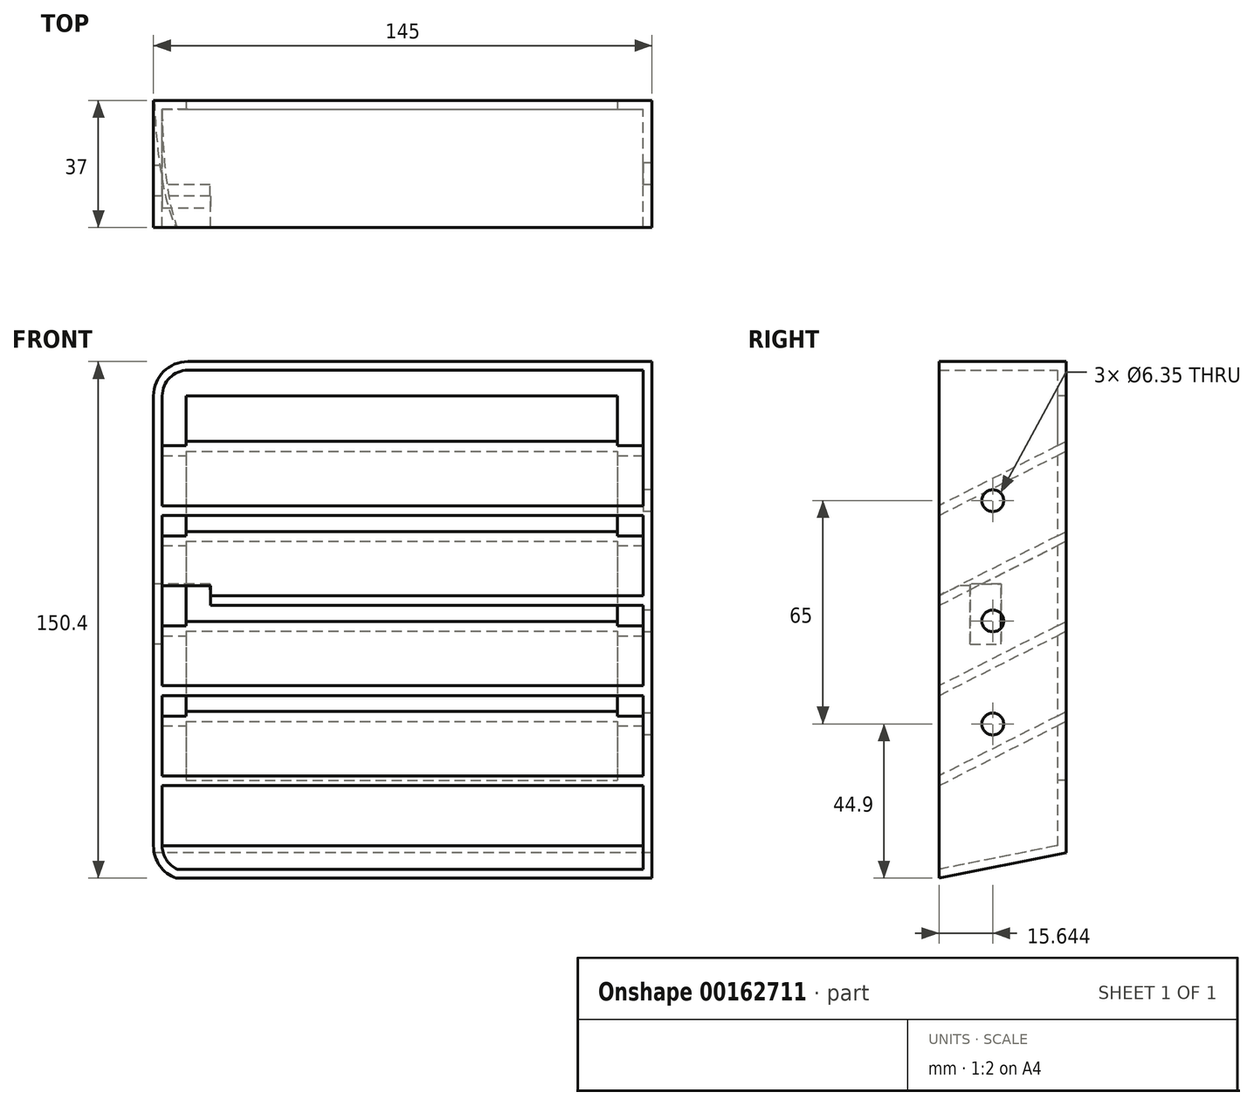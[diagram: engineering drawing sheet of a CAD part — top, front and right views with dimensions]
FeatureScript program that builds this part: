
annotation { "Feature Type Name" : "Feature", "Feature Type Description" : "" }
export const myFeature = defineFeature(function(context is Context, id is Id, definition is map)
    precondition{}
    {
        {
            var Q0;
            Q0=qCreatedBy(makeId("Front.planeOp"),FACE);
            var sketch = newSketch(context, id + "F0", { "sketchPlane" : qUnion([Q0])});
            skLineSegment(sketch, "E0.bottom", {"start": v(-62.5, 75.5) * mm, "end": v(72.5, 75.5) * mm});
            skLineSegment(sketch, "E0.top", {"start": v(-62.5, -75.5) * mm, "end": v(72.5, -75.5) * mm});
            skLineSegment(sketch, "E0.left", {"start": v(-72.5, 65.5) * mm, "end": v(-72.5, -65.5) * mm});
            skLineSegment(sketch, "E0.right", {"start": v(72.5, 75.5) * mm, "end": v(72.5, -75.5) * mm});
            skPoint(sketch, "E0.middle", {"position": v(0, 0) * mm});
            skPoint(sketch, "E1.visualSharp", {"position": v(72.5, 75.5) * mm});
            skPoint(sketch, "E2.visualSharp", {"position": v(72.5, -75.5) * mm});
            skPoint(sketch, "E3.visualSharp", {"position": v(-72.5, 75.5) * mm});
            skArc(sketch, "E3.filletArc", {"start": v(-62.5, 75.5) * mm, "mid": v(-69.57, 72.57) * mm, "end": v(-72.5, 65.5) * mm});
            skPoint(sketch, "E4.visualSharp", {"position": v(-72.5, -75.5) * mm});
            skArc(sketch, "E4.filletArc", {"start": v(-72.5, -65.5) * mm, "mid": v(-69.57, -72.57) * mm, "end": v(-62.5, -75.5) * mm});
            skSolve(sketch);
        }
        {
            var Q0;
            Q0=qSketchRegion(id+"F0",true);
            extrude(context, id + "F1", {"entities" : qUnion([Q0]), "depth" : 37 * mm});
        }
        {
            var Q0;
            Q0=makeQuery(id+"F1.opExtrude","CAP_EDGE",EDGE,{"disambiguationData":[OSD([sQuery(id+"F0.wireOp",EDGE,"E0.top")])],"isStart":true});
            chamfer(context, id + "F2", {"entities" : qUnion([Q0]), "chamferType" : ChamferType.TWO_OFFSETS, "width1" : 40 * mm, "oppositeDirection" : false, "width2" : 8 * mm});
        }
        {
            var Q0;
            Q0=makeQuery(id+"F1.opExtrude","CAP_FACE",FACE,{"disambiguationData":[OSD([sQuery(id+"F0.wireOp",EDGE,"E0.bottom"),sQuery(id+"F0.wireOp",EDGE,"E0.top"),sQuery(id+"F0.wireOp",EDGE,"E0.left"),sQuery(id+"F0.wireOp",EDGE,"E0.right"),sQuery(id+"F0.wireOp",EDGE,"E1.filletArc"),sQuery(id+"F0.wireOp",EDGE,"E2.filletArc")])],"isStart":false});
            shell(context, id + "F3", {"entities" : qUnion([Q0]), "thickness" : 2.54 * mm});
        }
        {
            var Q0;
            Q0=makeQuery(id+"F3.opShell","OFFSET_FACE",FACE,{"disambiguationData":[OSD([sQuery(id+"F0.wireOp",EDGE,"E0.bottom"),sQuery(id+"F0.wireOp",EDGE,"E0.top"),sQuery(id+"F0.wireOp",EDGE,"E0.left"),sQuery(id+"F0.wireOp",EDGE,"E0.right"),sQuery(id+"F0.wireOp",EDGE,"E1.filletArc"),sQuery(id+"F0.wireOp",EDGE,"E2.filletArc")])]});
            var sketch = newSketch(context, id + "F4", { "sketchPlane" : qUnion([Q0])});
            skPoint(sketch, "E5.middle", {"position": v(0, 0) * mm});
            skLineSegment(sketch, "E6.bottom", {"start": v(-63.05, 65.5) * mm, "end": v(62.5, 65.5) * mm});
            skLineSegment(sketch, "E6.top", {"start": v(-63.05, -46.42) * mm, "end": v(62.5, -46.42) * mm});
            skLineSegment(sketch, "E6.left", {"start": v(-63.05, 65.5) * mm, "end": v(-63.05, -46.42) * mm});
            skLineSegment(sketch, "E6.right", {"start": v(62.5, 65.5) * mm, "end": v(62.5, -46.42) * mm});
            skSolve(sketch);
        }
        {
            var Q0;
            Q0=makeQuery(id+"F4.imprint","IMPRINT",FACE,{"disambiguationData":[TD([[makeQuery(id+"F4.imprint","IMPRINT",EDGE,{"derivedFrom":sQuery(id+"F4.wireOp",EDGE,"E6.bottom")}),-1.0]])]});
            extrude(context, id + "F5", {"entities" : qUnion([Q0]), "operationType" : NewBodyOperationType.REMOVE, "oppositeDirection" : true, "depth" : 25.4 * mm});
        }
        {
            var Q0;
            Q0=makeQuery(id+"F3.opShell","OFFSET_FACE",FACE,{"disambiguationData":[OSD([sQuery(id+"F0.wireOp",EDGE,"E0.right")])]});
            var sketch = newSketch(context, id + "F6", { "sketchPlane" : qUnion([Q0])});
            skLineSegment(sketch, "E7.0.0", {"start": v(0, 75.5) * mm, "end": v(0, 75.5) * mm});
            skLineSegment(sketch, "E7.0.1", {"start": v(0, 75.5) * mm, "end": v(37, 75.5) * mm});
            skLineSegment(sketch, "E7.0.2", {"start": v(37, 75.5) * mm, "end": v(37, 75.5) * mm});
            skLineSegment(sketch, "E7.0.3", {"start": v(0, 75.5) * mm, "end": v(37, 75.5) * mm});
            skLineSegment(sketch, "E8.0.0", {"start": v(0, 65.5) * mm, "end": v(0, -67.5) * mm});
            skLineSegment(sketch, "E8.0.1", {"start": v(0, -67.5) * mm, "end": v(37, -75.5) * mm});
            skLineSegment(sketch, "E8.0.2", {"start": v(37, -75.5) * mm, "end": v(37, 65.5) * mm});
            skLineSegment(sketch, "E8.0.3", {"start": v(37, 65.5) * mm, "end": v(0, 65.5) * mm});
            skCircle(sketch, "E9", {"center": v(21.36, 0) * mm, "radius": 3.18 * mm});
            skCircle(sketch, "E10.0.1.0", {"center": v(21.36, -30) * mm, "radius": 3.18 * mm});
            skLineSegment(sketch, "E10.direction2", {"start": v(21.36, 0) * mm, "end": v(21.36, -30) * mm, "construction": true});
            skCircle(sketch, "E11", {"center": v(21.36, 35) * mm, "radius": 3.18 * mm});
            skSolve(sketch);
        }
        {
            var Q0;
            Q0=makeQuery(id+"F6.imprint","IMPRINT",FACE,{"disambiguationData":[TD([[makeQuery(id+"F6.imprint","IMPRINT",EDGE,{"derivedFrom":sQuery(id+"F6.wireOp",EDGE,"E9")}),1.0]])]});
            var Q1;
            Q1=makeQuery(id+"F6.imprint","IMPRINT",FACE,{"disambiguationData":[TD([[makeQuery(id+"F6.imprint","IMPRINT",EDGE,{"derivedFrom":sQuery(id+"F6.wireOp",EDGE,"E11")}),1.0]])]});
            var Q2;
            Q2=makeQuery(id+"F6.imprint","IMPRINT",FACE,{"disambiguationData":[TD([[makeQuery(id+"F6.imprint","IMPRINT",EDGE,{"derivedFrom":sQuery(id+"F6.wireOp",EDGE,"E10.0.1.0")}),1.0]])]});
            var Q3;
            Q3=sQuery(id+"F6.wireOp",EDGE,"E11");
            var Q4;
            Q4=sQuery(id+"F6.wireOp",EDGE,"E9");
            var Q5;
            Q5=sQuery(id+"F6.wireOp",EDGE,"E10.0.1.0");
            extrude(context, id + "F7", {"entities" : qUnion([Q0, Q1, Q2]), "operationType" : NewBodyOperationType.REMOVE, "surfaceEntities" : qUnion([Q3, Q4, Q5]), "oppositeDirection" : true, "depth" : 19.05 * mm});
        }
        {
            var Q0;
            Q0=makeQuery(id+"F3.opShell","OFFSET_FACE",FACE,{"disambiguationData":[OSD([sQuery(id+"F0.wireOp",EDGE,"E0.right")])]});
            var sketch = newSketch(context, id + "F8", { "sketchPlane" : qUnion([Q0])});
            skLineSegment(sketch, "E12", {"start": v(37, -47.95) * mm, "end": v(0, -29.24) * mm});
            skLineSegment(sketch, "E13", {"start": v(0, -29.24) * mm, "end": v(0, -26.39) * mm});
            skLineSegment(sketch, "E14", {"start": v(0, -26.39) * mm, "end": v(37, -45.1) * mm});
            skLineSegment(sketch, "E15", {"start": v(37, -45.1) * mm, "end": v(37, -47.95) * mm});
            skLineSegment(sketch, "E16", {"start": v(37, -21.74) * mm, "end": v(0, -3.02) * mm});
            skLineSegment(sketch, "E17", {"start": v(0, -3.02) * mm, "end": v(0, -0.17) * mm});
            skLineSegment(sketch, "E18", {"start": v(0, -0.17) * mm, "end": v(37, -18.9) * mm});
            skLineSegment(sketch, "E19", {"start": v(37, -18.9) * mm, "end": v(37, -21.74) * mm});
            skLineSegment(sketch, "E20", {"start": v(37, 4.48) * mm, "end": v(0, 23.2) * mm});
            skLineSegment(sketch, "E21", {"start": v(0, 23.2) * mm, "end": v(0, 26.04) * mm});
            skLineSegment(sketch, "E22", {"start": v(0, 26.04) * mm, "end": v(37, 7.32) * mm});
            skLineSegment(sketch, "E23", {"start": v(37, 7.32) * mm, "end": v(37, 4.48) * mm});
            skLineSegment(sketch, "E24", {"start": v(37, 30.7) * mm, "end": v(0, 49.4) * mm});
            skLineSegment(sketch, "E25", {"start": v(0, 49.4) * mm, "end": v(0, 52.25) * mm});
            skLineSegment(sketch, "E26", {"start": v(0, 52.25) * mm, "end": v(37, 33.54) * mm});
            skLineSegment(sketch, "E27", {"start": v(37, 33.54) * mm, "end": v(37, 30.7) * mm});
            skSolve(sketch);
        }
        {
            var Q0;
            Q0 = qSketchRegion(id + "F8", true);
            extrude(context, id + "F9", {"entities" : qUnion([Q0]), "operationType" : NewBodyOperationType.ADD, "depth" : 142.24 * mm});
        }
        {
            var Q0;
            Q0=makeQuery(id+"F1.opExtrude","SWEPT_FACE",FACE,{"disambiguationData":[OSD([sQuery(id+"F0.wireOp",EDGE,"E0.left")])]});
            var sketch = newSketch(context, id + "F10", { "sketchPlane" : qUnion([Q0])});
            skLineSegment(sketch, "E28.bottom", {"start": v(18.9, 10.75) * mm, "end": v(27.9, 10.75) * mm});
            skLineSegment(sketch, "E28.top", {"start": v(18.9, -6.75) * mm, "end": v(27.9, -6.75) * mm});
            skLineSegment(sketch, "E28.left", {"start": v(18.9, 10.75) * mm, "end": v(18.9, -6.75) * mm});
            skLineSegment(sketch, "E28.right", {"start": v(27.9, 10.75) * mm, "end": v(27.9, -6.75) * mm});
            skSolve(sketch);
        }
        {
            var Q0;
            Q0=makeQuery(id+"F10.imprint","IMPRINT",FACE,{"disambiguationData":[TD([[makeQuery(id+"F10.imprint","IMPRINT",EDGE,{"derivedFrom":sQuery(id+"F10.wireOp",EDGE,"E28.bottom")}),-1.0]])]});
            var Q1;
            Q1 = qSketchRegion(id + "FNYe9KNpvqW2HJJ_1", true);
            extrude(context, id + "F11", {"entities" : qUnion([Q0, Q1]), "operationType" : NewBodyOperationType.REMOVE, "oppositeDirection" : true, "depth" : 16.5 * mm});
        }
        {
            var Q0;
            {var subQ3=sQuery(id+"F0.wireOp",EDGE,"E0.left");Q0=makeQuery(id+"F9.boolean.opBoolean","SPLIT",FACE,{"disambiguationData":[TD([makeQuery(id+"F9.opExtrude","SWEPT_FACE",FACE,{"disambiguationData":[OSD([sQuery(id+"F8.wireOp",EDGE,"E18")])]})])],"derivedFrom":makeQuery(id+"F3.opShell","OFFSET_FACE",FACE,{"disambiguationData":[OSD([subQ3])]})});}
            var sketch = newSketch(context, id + "F12", { "sketchPlane" : qUnion([Q0])});
            skLineSegment(sketch, "E29.bottom", {"start": v(-27.9, -6.75) * mm, "end": v(-44.66, -6.75) * mm});
            skLineSegment(sketch, "E29.top", {"start": v(-27.9, 10.22) * mm, "end": v(-44.66, 10.22) * mm});
            skLineSegment(sketch, "E29.left", {"start": v(-27.9, -6.75) * mm, "end": v(-27.9, 10.22) * mm});
            skLineSegment(sketch, "E29.right", {"start": v(-44.66, -6.75) * mm, "end": v(-44.66, 10.22) * mm});
            skSolve(sketch);
        }
        {
            var Q0;
            {var subQ11=sQuery(id+"F12.wireOp",EDGE,"E29.top");Q0=makeQuery(id+"F12.imprint","IMPRINT",FACE,{"disambiguationData":[TD([[makeQuery(id+"F12.imprint","IMPRINT",EDGE,{"derivedFrom":subQ11}),1.0]])]});}
            extrude(context, id + "F13", {"entities" : qUnion([Q0]), "operationType" : NewBodyOperationType.REMOVE, "depth" : 14 * mm});
        }
    });
